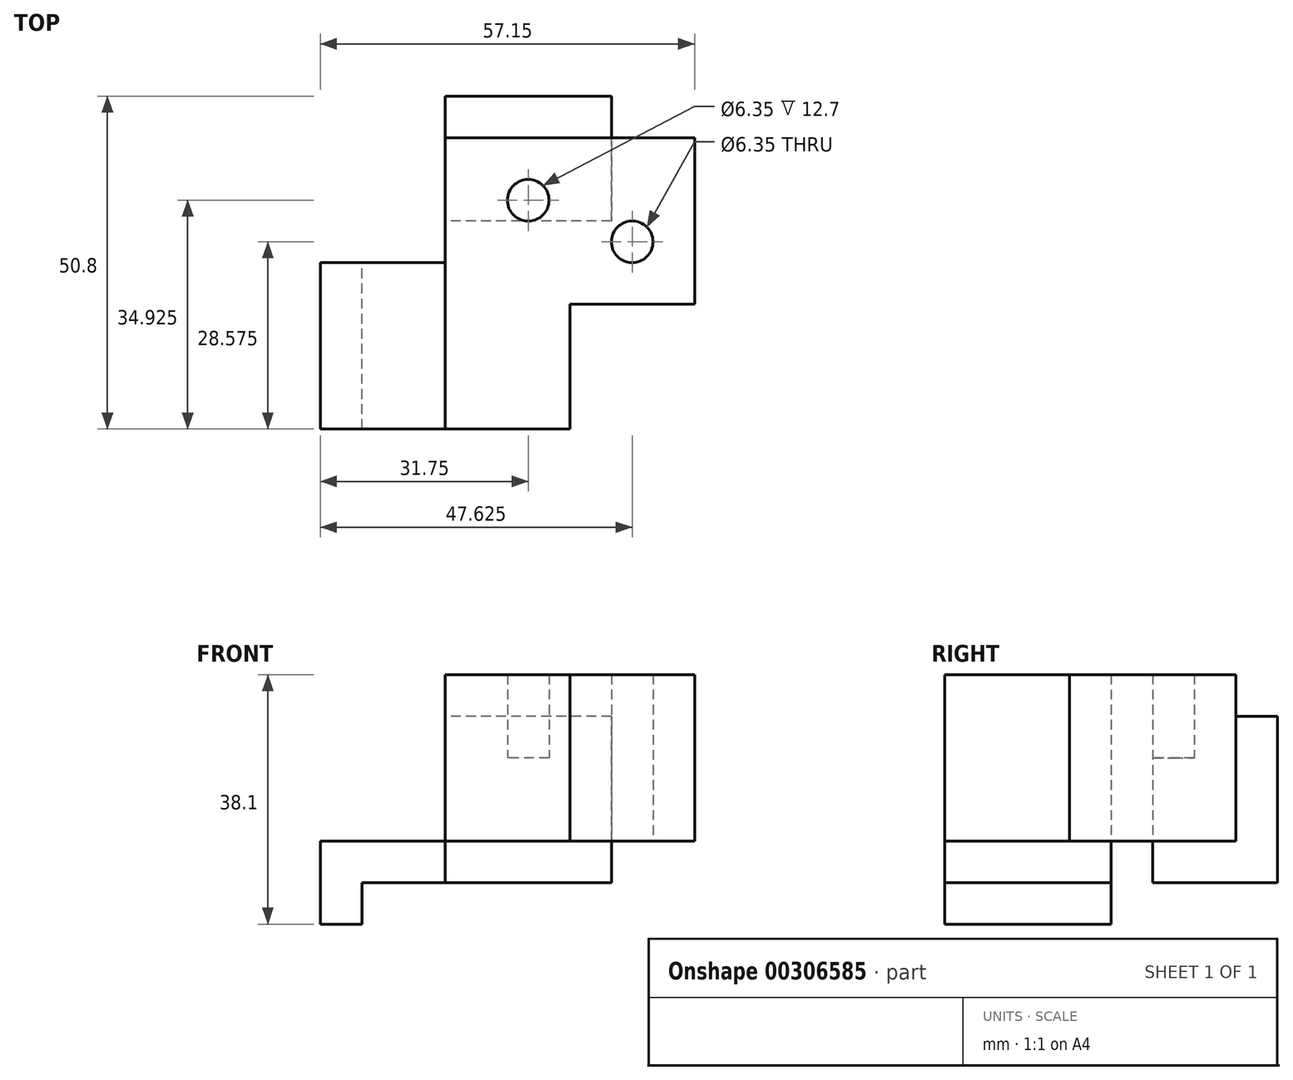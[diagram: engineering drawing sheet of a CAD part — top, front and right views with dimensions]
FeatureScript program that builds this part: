
annotation { "Feature Type Name" : "Feature", "Feature Type Description" : "" }
export const myFeature = defineFeature(function(context is Context, id is Id, definition is map)
    precondition{}
    {
        {
            var Q0;
            Q0=qCreatedBy(makeId("Top.planeOp"),FACE);
            var sketch = newSketch(context, id + "F0", { "sketchPlane" : qUnion([Q0])});
            skLineSegment(sketch, "E0.bottom", {"start": v(0, 0) * mm, "end": v(19.05, 0) * mm});
            skLineSegment(sketch, "E0.top", {"start": v(0, 19.05) * mm, "end": v(19.05, 19.05) * mm});
            skLineSegment(sketch, "E0.left", {"start": v(0, 0) * mm, "end": v(0, 19.05) * mm});
            skLineSegment(sketch, "E0.right", {"start": v(19.05, 0) * mm, "end": v(19.05, 19.05) * mm});
            skLineSegment(sketch, "E1.bottom", {"start": v(19.05, 19.05) * mm, "end": v(38.1, 19.05) * mm});
            skLineSegment(sketch, "E1.top", {"start": v(19.05, 12.7) * mm, "end": v(38.1, 12.7) * mm});
            skLineSegment(sketch, "E1.left", {"start": v(19.05, 19.05) * mm, "end": v(19.05, 12.7) * mm});
            skLineSegment(sketch, "E1.right", {"start": v(38.1, 19.05) * mm, "end": v(38.1, 12.7) * mm});
            skLineSegment(sketch, "E2.bottom", {"start": v(38.1, 12.7) * mm, "end": v(19.05, 12.7) * mm});
            skLineSegment(sketch, "E2.top", {"start": v(38.1, -6.35) * mm, "end": v(19.05, -6.35) * mm});
            skLineSegment(sketch, "E2.left", {"start": v(38.1, 12.7) * mm, "end": v(38.1, -6.35) * mm});
            skLineSegment(sketch, "E2.right", {"start": v(19.05, 12.7) * mm, "end": v(19.05, -6.35) * mm});
            skCircle(sketch, "E3", {"center": v(28.58, 3.17) * mm, "radius": 3.18 * mm});
            skCircle(sketch, "E4", {"center": v(12.7, 9.53) * mm, "radius": 3.18 * mm});
            skPoint(sketch, "E4.centerSnap0", {"position": v(19.05, 9.52) * mm});
            skSolve(sketch);
        }
        {
            var Q0;
            Q0=qCreatedBy(makeId("Front.planeOp"),FACE);
            var sketch = newSketch(context, id + "F1", { "sketchPlane" : qUnion([Q0])});
            skLineSegment(sketch, "E5.bottom", {"start": v(0, 0) * mm, "end": v(19.05, 0) * mm});
            skLineSegment(sketch, "E6", {"start": v(0, 0) * mm, "end": v(-19.05, 0) * mm});
            skLineSegment(sketch, "E7", {"start": v(-19.05, 0) * mm, "end": v(-19.05, -12.7) * mm});
            skLineSegment(sketch, "E8", {"start": v(-19.05, -12.7) * mm, "end": v(-12.7, -12.7) * mm});
            skLineSegment(sketch, "E9", {"start": v(-12.7, -12.7) * mm, "end": v(-12.7, -6.35) * mm});
            skLineSegment(sketch, "E10", {"start": v(-12.7, -6.35) * mm, "end": v(0, -6.35) * mm});
            skLineSegment(sketch, "E11", {"start": v(0, -6.35) * mm, "end": v(0, 0) * mm});
            skLineSegment(sketch, "E12.top", {"start": v(0, 25.4) * mm, "end": v(19.05, 25.4) * mm});
            skLineSegment(sketch, "E12.left", {"start": v(0, 0) * mm, "end": v(0, 25.4) * mm});
            skLineSegment(sketch, "E12.right", {"start": v(19.05, 0) * mm, "end": v(19.05, 25.4) * mm});
            skLineSegment(sketch, "E13.top", {"start": v(0, 19.05) * mm, "end": v(19.05, 19.05) * mm});
            skLineSegment(sketch, "E13.left", {"start": v(0, 25.4) * mm, "end": v(0, 19.05) * mm});
            skLineSegment(sketch, "E13.right", {"start": v(19.05, 25.4) * mm, "end": v(19.05, 19.05) * mm});
            skSolve(sketch);
        }
        {
            var Q0;
            Q0=qCreatedBy(makeId("Right.planeOp"),FACE);
            var sketch = newSketch(context, id + "F2", { "sketchPlane" : qUnion([Q0])});
            skLineSegment(sketch, "E14", {"start": v(0, 0) * mm, "end": v(0, 12.7) * mm});
            skLineSegment(sketch, "E15", {"start": v(0, 12.7) * mm, "end": v(19.05, 12.7) * mm});
            skLineSegment(sketch, "E16", {"start": v(19.05, 12.7) * mm, "end": v(19.05, 19.05) * mm});
            skLineSegment(sketch, "E17", {"start": v(19.05, 19.05) * mm, "end": v(25.4, 19.05) * mm});
            skLineSegment(sketch, "E18", {"start": v(25.4, 19.05) * mm, "end": v(25.4, -6.35) * mm});
            skLineSegment(sketch, "E19", {"start": v(25.4, -6.35) * mm, "end": v(6.35, -6.35) * mm});
            skLineSegment(sketch, "E20", {"start": v(6.35, -6.35) * mm, "end": v(6.35, 0) * mm});
            skLineSegment(sketch, "E21", {"start": v(6.35, 0) * mm, "end": v(0, 0) * mm});
            skLineSegment(sketch, "E22", {"start": v(6.35, 0) * mm, "end": v(25.4, 0) * mm});
            skSolve(sketch);
        }
        {
            var Q0;
            Q0 = qSketchRegion(id + "F0", true);
            extrude(context, id + "F3", {"entities" : qUnion([Q0]), "depth" : 25.4 * mm});
        }
        {
            var Q0;
            Q0 = qSketchRegion(id + "F1", true);
            extrude(context, id + "F4", {"entities" : qUnion([Q0]), "operationType" : NewBodyOperationType.ADD, "depth" : 25.4 * mm});
        }
        {
            var Q0;
            Q0 = qSketchRegion(id + "F2", true);
            extrude(context, id + "F5", {"entities" : qUnion([Q0]), "operationType" : NewBodyOperationType.ADD, "depth" : 25.4 * mm});
        }
    });
